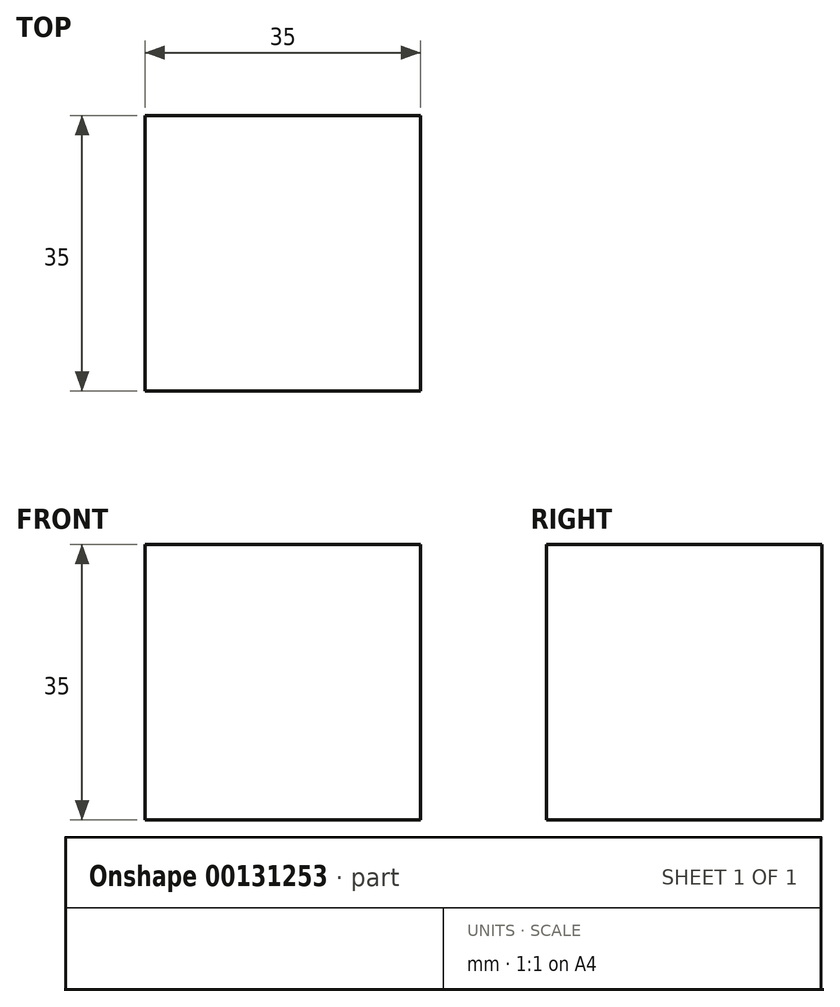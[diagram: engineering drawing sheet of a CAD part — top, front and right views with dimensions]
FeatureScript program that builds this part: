
annotation { "Feature Type Name" : "Feature", "Feature Type Description" : "" }
export const myFeature = defineFeature(function(context is Context, id is Id, definition is map)
    precondition{}
    {
        {
            var Q0;
            Q0=qCreatedBy(makeId("Top.planeOp"),FACE);
            var sketch = newSketch(context, id + "F0", { "sketchPlane" : qUnion([Q0])});
            skLineSegment(sketch, "E0.bottom", {"start": v(-20.86, 19.66) * mm, "end": v(14.14, 19.66) * mm});
            skLineSegment(sketch, "E0.top", {"start": v(-20.86, -15.34) * mm, "end": v(14.14, -15.34) * mm});
            skLineSegment(sketch, "E0.left", {"start": v(-20.86, 19.66) * mm, "end": v(-20.86, -15.34) * mm});
            skLineSegment(sketch, "E0.right", {"start": v(14.14, 19.66) * mm, "end": v(14.14, -15.34) * mm});
            skSolve(sketch);
        }
        {
            var Q0;
            Q0=makeQuery(id+"F0.imprint","IMPRINT",FACE,{"disambiguationData":[TD([[makeQuery(id+"F0.imprint","IMPRINT",EDGE,{"derivedFrom":sQuery(id+"F0.wireOp",EDGE,"E0.bottom")}),-1.0]])]});
            extrude(context, id + "F1", {"entities" : qUnion([Q0]), "depth" : 35 * mm});
        }
    });
